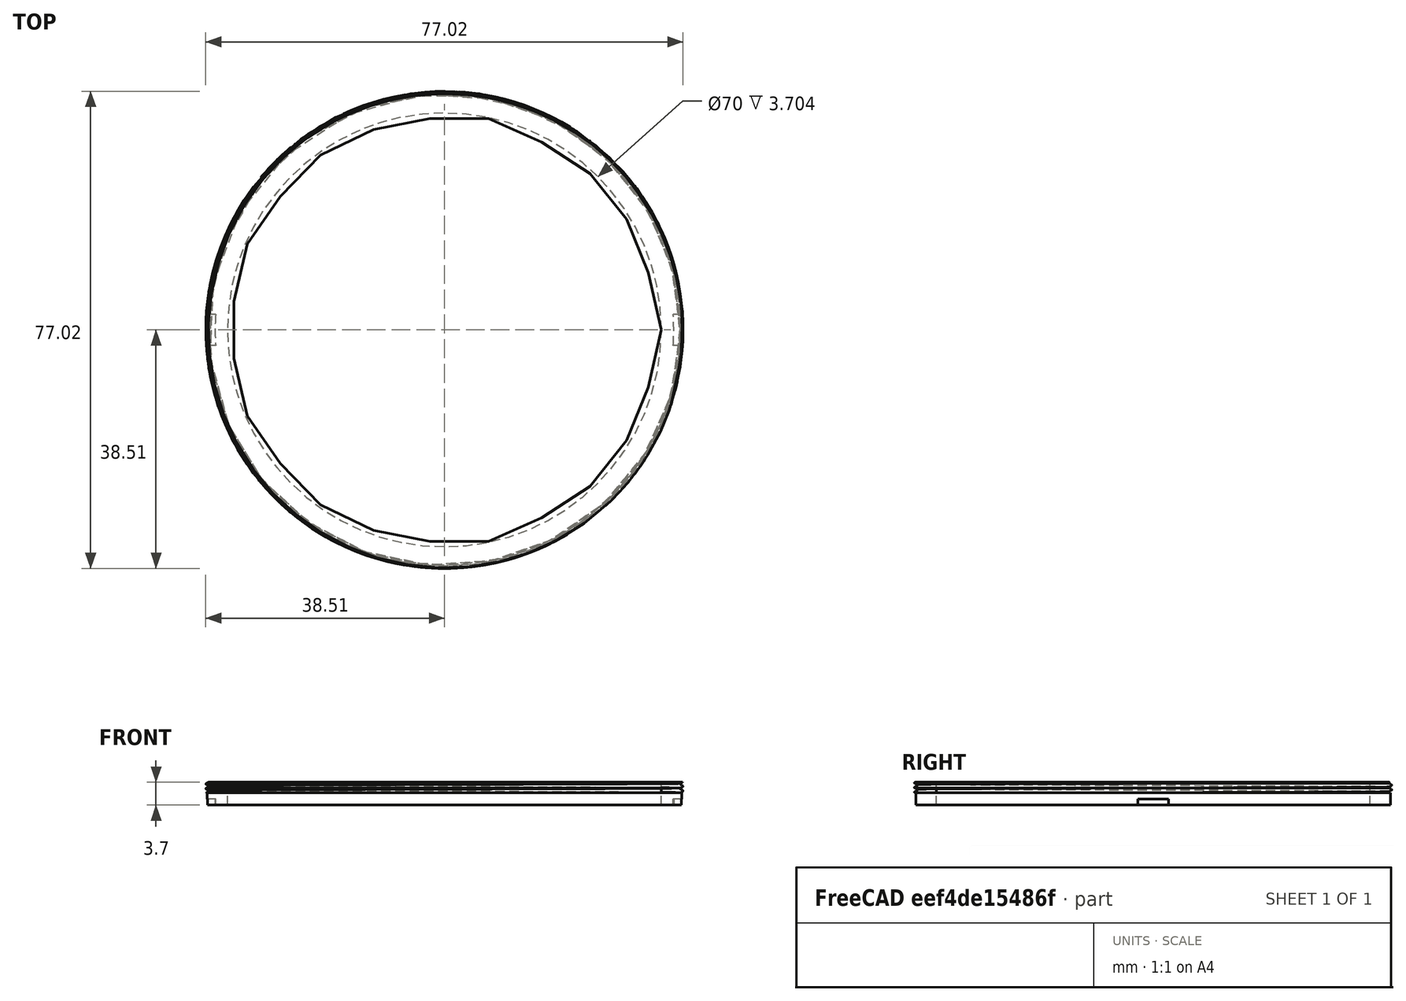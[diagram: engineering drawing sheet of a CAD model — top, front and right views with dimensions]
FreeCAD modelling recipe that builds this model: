
FCSTD DOCUMENT  (FreeCAD 2021.717R24301 +3627 (Git))
Label: M77 Bahtinov mask
License: All rights reserved
LicenseURL: http://en.wikipedia.org/wiki/All_rights_reserved
objects: Sketcher::SketchObject×3, PartDesign::Body×2, PartDesign::Pad×2, Mesh::Feature×2, Part::Part2DObjectPython×1, PartDesign::AdditiveHelix×1, PartDesign::Pocket×1, Part::MultiFuse×1, Part::Cylinder×1, Part::Cut×1
note: 21 computed .brp shape members not serialized (recipe doc carries the construction recipe); baked Part::Feature solids carry a one-line shape summary decoded from their .brp

FEATURE [Part::Part2DObjectPython] VThreadProfile  # Draft 2D object (typed FeaturePython)
  Area = 4600.76
  Closed = true
  Continuity = C3
  Instructions = Expand this with the ... button to view instructions | Sweep this object along a helix of the same pitch to produce your thread. | It is recommended to make the helix in the ThreadProfile workbench. | If there is an active Body the ThreadProfile object will be put into it.,If not it can be dragged and dropped into the body later. | If there is an active Body when the helix is made there will be made a ShapeBinder for it | For internal threads you will need to cut the Sweep object out of a cylinder, or if using Part Design sweep it as a Subtractive Pipe. | Always use Frenet mode | I have provided some presets, but it is possible there could be some errors.  Double check for mission critical applications. | Also, the tolerances might be different from what you wish to have.  I believe the internal minor diameters are all minimum and the external are all maximum.
  InternalOrExternal = 1
  MakeFace = true
  MinorDiameter = 76.2
  Parameterization = 1
  Pitch = 0.75
  Points = (719) [(38.0968,0.332928,0),(38.0907,0.665801,0),(38.0818,0.998595,0),(38.0701,1.33129,0),(38.0555,1.66385,0),(38.038,1.99627,0),(38.0177,2.32851,0),+712 more]
  Presets = 0
  Quality = 1
  ThreadCount = 10
  Version = 1.69
  external_data = [-0.00235387,-0.00461052,-0.00677828,-0.00886428,-0.0108747,-0.0128149,-0.0146895,-0.0165028,-0.0182584,-0.0199597,-0.0216095,-0.0232106,-0.0247653,-0.0262759,-0.0277444,-0.0291725,-0.0305621,-0.0319145,-0.0332313,-0.0345138,-0.0357632,+698 more]
  internal_data = [0,0,0,0,0,0,0,0,0,0,0,0,0,0,0,0,0,0,0,0,0,0,0,0,0,0,0,0,0,0,0,0,0,0,0,0,0,0,0,0,0,0,0,0,0,0,0,0,0,0,0,0,0,0,0,0,0,0,0,0,0,0,0,0,0,0,0,0,0,0,0,0,0,0,0,0,0,0,0,0,0,0,0,0,0,0,0,0,0,0,0,0,0,0,0,0,0,0,0,0,0,0,0,0,0,0,0,0,0,0,0,0,0,0,0,0,0,0,0,0,+599 more]
  preset_names = <blob: 3959 chars omitted>
  presets_data = [0,0,0,2.20878,24.1173,24.6888,0.25,0.693,0.729,0.25,0.793,0.829,0.25,0.893,0.929,0.3,1.032,1.075,0.35,1.171,1.221,0.35,1.371,1.421,0.4,1.509,1.567,0.45,1.648,1.713,0.45,1.948,2.013,0.5,2.387,2.459,0.6,2.764,2.85,0.7,3.141,3.242,0.75,3.58,+712 more]
FEATURE [PartDesign::AdditiveHelix] AdditiveHelix
  Angle = 0
  Axis = (-3e-16,3e-16,1)
  Base = (0,0,0)
  ClaimChildren = false
  Fit = 0
  FitJoin = 0
  HasBeenEdited = true
  Height = 1.7
  InnerFit = 0
  InnerFitJoin = 0
  LeftHanded = false
  Mode = 0
  NewSolid = false
  Outside = false
  Pitch = 0.75
  Profile = -> VThreadProfile
  ReferenceAxis = -> Z_Axis
  Refine = true
  Suppress = false
  Turns = 3
  _ProfileBasedVersion = 1
FEATURE [PartDesign::Body] Body
  AutoGroupSolids = false
  ExportMode = 0
  Group = -> [VThreadProfile,AdditiveHelix]
  Origin = -> Origin
  Placement = pos=(0,0,2) rot=(0,0,1;0rad)
  Tip = -> AdditiveHelix
  _ExportChildren = -> [AdditiveHelix]
  _GroupVersion = 1
FEATURE [Sketcher::SketchObject] Sketch
  FullyConstrained = true
  MapMode = 5
  Support = -> [XY_Plane002]
  sketch-geometry (1):
    g0: Circle CenterX=0 CenterY=0 CenterZ=0 NormalX=0 NormalY=0 NormalZ=1 AngleXU=0 Radius=38.3
  constraints (2):
    c: Coincident(g0,g-1)
    c: Diameter(g0) = 76.6
FEATURE [PartDesign::Pad] Pad
  ClaimChildren = false
  Direction = (1,1,1)
  Fit = 0
  FitJoin = 0
  InnerFit = 0
  InnerFitJoin = 0
  InnerTaperAngle = 0
  InnerTaperAngleRev = 0
  Length = 2
  Length2 = 100
  Linearize = true
  NewSolid = false
  Profile = -> Sketch
  Refine = true
  Suppress = false
  Type = 0
  _ProfileBasedVersion = 1
FEATURE [Sketcher::SketchObject] Sketch001
  FullyConstrained = true
  MapMode = 5
  Placement = pos=(0,0,0) rot=(0,1,0;3.14159rad)
  Support = -> [XY_Plane002]
  sketch-geometry (10):
    g0: ArcOfCircle CenterX=0 CenterY=-2.39e-14 CenterZ=0 NormalX=0 NormalY=0 NormalZ=1 AngleXU=0 Radius=37 StartAngle=3.07397 EndAngle=3.20921
    g1: LineSegment [constr] StartX=-36.9154 StartY=2.5 StartZ=0 EndX=36.9154 EndY=2.5 EndZ=0
    g2: LineSegment [constr] StartX=36.9154 StartY=-2.5 StartZ=0 EndX=-36.9154 EndY=-2.5 EndZ=0
    g3: ArcOfCircle CenterX=0 CenterY=-2.39e-14 CenterZ=0 NormalX=0 NormalY=0 NormalZ=1 AngleXU=0 Radius=37 StartAngle=6.21557 EndAngle=6.3508
    g4: ArcOfCircle CenterX=0 CenterY=-2.39e-14 CenterZ=0 NormalX=0 NormalY=0 NormalZ=1 AngleXU=0 Radius=38.5 StartAngle=6.2182 EndAngle=6.34817
    g5: ArcOfCircle CenterX=0 CenterY=-2.39e-14 CenterZ=0 NormalX=0 NormalY=0 NormalZ=1 AngleXU=0 Radius=38.5 StartAngle=3.07661 EndAngle=3.20657
    g6: LineSegment StartX=-38.4187 StartY=2.5 StartZ=0 EndX=-36.9154 EndY=2.5 EndZ=0
    g7: LineSegment StartX=-38.4187 StartY=-2.5 StartZ=0 EndX=-36.9154 EndY=-2.5 EndZ=0
    g8: LineSegment StartX=36.9154 StartY=-2.5 StartZ=0 EndX=38.4187 EndY=-2.5 EndZ=0
    g9: LineSegment StartX=36.9154 StartY=2.5 StartZ=0 EndX=38.4187 EndY=2.5 EndZ=0
  constraints (28):
    c: Diameter(g0) = 74
    c: Horizontal(g1)
    c: Horizontal(g2)
    c: Symmetric(g2,g1,g-1)
    c: DistanceY(g2,g1) = 5
    c: Coincident(g0,g1)
    c: Coincident(g3,g1)
    c: Equal(g0,g3)
    c: Coincident(g0,g2)
    c: Coincident(g3,g2)
    c: Coincident(g0,g3)
    c: Coincident(g0,g-1)
    c: Coincident(g4,g0)
    c: Coincident(g5,g0)
    c: Equal(g5,g4)
    c: Diameter(g4) = 77
    c: Coincident(g6,g5)
    c: Coincident(g6,g0)
    c: Coincident(g7,g5)
    c: Coincident(g7,g0)
    c: Coincident(g8,g3)
    c: Coincident(g8,g4)
    c: Coincident(g9,g3)
    c: Coincident(g9,g4)
    c: Horizontal(g6)
    c: Horizontal(g7)
    c: Horizontal(g8)
    c: Horizontal(g9)
FEATURE [PartDesign::Pocket] Pocket
  BaseFeature = -> Pad
  ClaimChildren = false
  Fit = 0
  FitJoin = 0
  InnerFit = 0
  InnerFitJoin = 0
  InnerTaperAngle = 0
  InnerTaperAngleRev = 0
  Length = 1
  Length2 = 100
  Linearize = true
  NewSolid = false
  Profile = -> Sketch001
  Refine = true
  Suppress = false
  Type = 0
  _ProfileBasedVersion = 1
FEATURE [Sketcher::SketchObject] Sketch002
  AttachmentOffset = pos=(0,0,0.8) rot=(0,0,1;0rad)
  FullyConstrained = true
  MapMode = 5
  Placement = pos=(0,0,0.8) rot=(0,0,1;0rad)
  Support = -> [XY_Plane002]
  sketch-geometry (1):
    g0: Circle CenterX=0 CenterY=0 CenterZ=0 NormalX=0 NormalY=0 NormalZ=1 AngleXU=0 Radius=25.4
  constraints (2):
    c: Diameter(g0) = 50.8
    c: Coincident(g0,g-1)
FEATURE [PartDesign::Pad] Pad001
  BaseFeature = -> Pocket
  ClaimChildren = false
  Direction = (1,1,1)
  Fit = 0
  FitJoin = 0
  InnerFit = 0
  InnerFitJoin = 0
  InnerTaperAngle = 0
  InnerTaperAngleRev = 0
  Length = 1.2
  Length2 = 100
  Linearize = true
  NewSolid = false
  Profile = -> Sketch002
  Refine = true
  Suppress = false
  Type = 0
  _ProfileBasedVersion = 1
FEATURE [PartDesign::Body] Body002
  AutoGroupSolids = false
  ExportMode = 0
  Group = -> [Sketch,Pad,Sketch001,Pocket,Sketch002,Pad001]
  Origin = -> Origin002
  Tip = -> Pad001
  _ExportChildren = -> [Pad,Pocket,Pad001]
  _GroupVersion = 1
FEATURE [Part::MultiFuse] Fusion
  Refine = true
  Shapes = -> [Body,Body002]
FEATURE [Part::Cylinder] Cylinder
  Angle = 360
  AttacherType = Attacher::AttachEngine3D
  Height = 10
  Radius = 35
FEATURE [Part::Cut] Cut
  Base = -> Fusion
  Refine = true
  Tool = -> Cylinder
FEATURE [Mesh::Feature] bahtinov_70_180mm  label="bahtinov-70-180mm"
FEATURE [Mesh::Feature] bahtinov_70  label="bahtinov-70-70mm"
